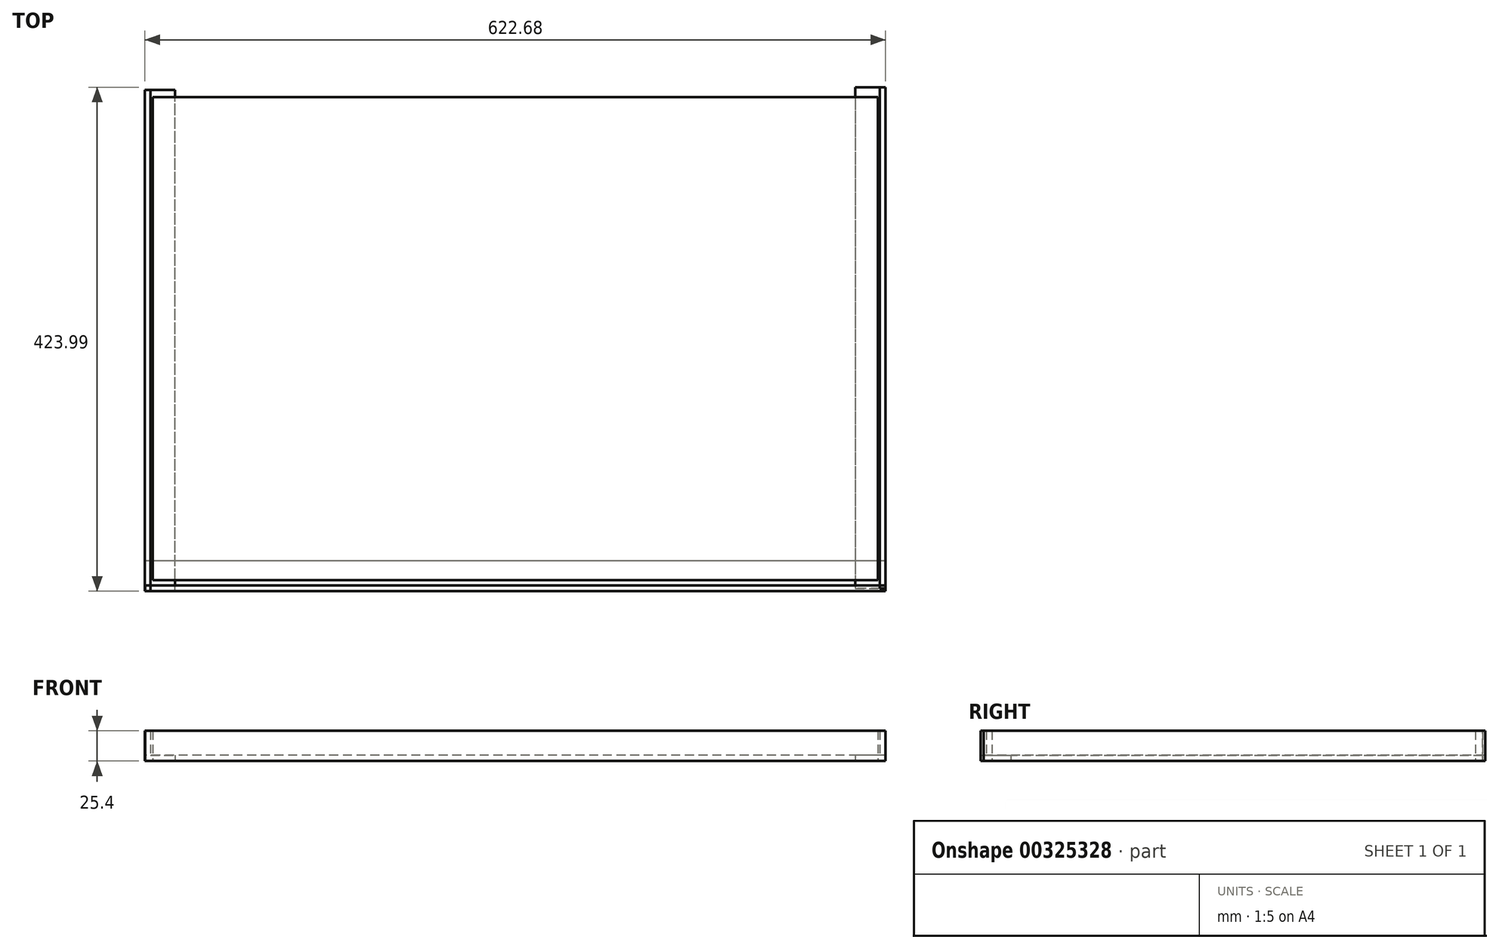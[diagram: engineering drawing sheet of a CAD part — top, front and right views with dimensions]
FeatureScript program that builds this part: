
annotation { "Feature Type Name" : "Feature", "Feature Type Description" : "" }
export const myFeature = defineFeature(function(context is Context, id is Id, definition is map)
    precondition{}
    {
        {
            var Q0;
            Q0=qCreatedBy(makeId("Right.planeOp"),FACE);
            var sketch = newSketch(context, id + "F0", { "sketchPlane" : qUnion([Q0])});
            skLineSegment(sketch, "E0", {"start": v(0, 0) * mm, "end": v(0, 25.4) * mm});
            skLineSegment(sketch, "E1", {"start": v(0, 25.4) * mm, "end": v(4.76, 25.4) * mm});
            skLineSegment(sketch, "E2", {"start": v(4.76, 25.4) * mm, "end": v(4.76, 4.76) * mm});
            skLineSegment(sketch, "E3", {"start": v(4.76, 4.76) * mm, "end": v(25.4, 4.76) * mm});
            skLineSegment(sketch, "E4", {"start": v(25.4, 4.76) * mm, "end": v(25.4, 0) * mm});
            skLineSegment(sketch, "E5", {"start": v(25.4, 0) * mm, "end": v(0, 0) * mm});
            skSolve(sketch);
        }
        {
            var Q0;
            Q0=makeQuery(id+"F0.imprint","IMPRINT",FACE,{"disambiguationData":[TD([[makeQuery(id+"F0.imprint","IMPRINT",EDGE,{"derivedFrom":sQuery(id+"F0.wireOp",EDGE,"E0")}),-1.0]])]});
            extrude(context, id + "F1", {"entities" : qUnion([Q0]), "endBound" : BoundingType.SYMMETRIC, "depth" : 622.3 * mm});
        }
        {
            var Q0;
            Q0=makeQuery(id+"F0.imprint","IMPRINT",FACE,{"disambiguationData":[TD([[makeQuery(id+"F0.imprint","IMPRINT",EDGE,{"derivedFrom":sQuery(id+"F0.wireOp",EDGE,"E0")}),-1.0]])]});
            extrude(context, id + "F2", {"entities" : qUnion([Q0]), "endBound" : BoundingType.SYMMETRIC, "depth" : 421.64 * mm});
        }
        {
            var Q0;
            Q0=makeQuery(id+"F2.opExtrude","SWEPT_BODY",BODY,{"disambiguationData":[OSD([sQuery(id+"F0.wireOp",EDGE,"E0"),sQuery(id+"F0.wireOp",EDGE,"E1"),sQuery(id+"F0.wireOp",EDGE,"E2"),sQuery(id+"F0.wireOp",EDGE,"E3"),sQuery(id+"F0.wireOp",EDGE,"E4"),sQuery(id+"F0.wireOp",EDGE,"E5")])]});
            var Q1;
            Q1=sQuery(id+"F0.wireOp",EDGE,"E2");
            transform(context, id + "F3", {"entities" : qUnion([Q0]), "transformType" : TransformType.ROTATION, "transformAxis" : qUnion([Q1]), "angle" : 90 * degree, "makeCopy" : false});
        }
        {
            var Q0;
            Q0=makeQuery(id+"F2.opExtrude","SWEPT_BODY",BODY,{"disambiguationData":[OSD([sQuery(id+"F0.wireOp",EDGE,"E0"),sQuery(id+"F0.wireOp",EDGE,"E1"),sQuery(id+"F0.wireOp",EDGE,"E2"),sQuery(id+"F0.wireOp",EDGE,"E3"),sQuery(id+"F0.wireOp",EDGE,"E4"),sQuery(id+"F0.wireOp",EDGE,"E5")])]});
            transform(context, id + "F4", {"entities" : qUnion([Q0]), "transformType" : TransformType.TRANSLATION_3D, "dx" : -306.58 * mm, "dy" : 0 * mm, "dz" : 0 * mm, "makeCopy" : false});
        }
        {
            var Q0;
            Q0=makeQuery(id+"F1.opExtrude","SWEPT_BODY",BODY,{"disambiguationData":[OSD([sQuery(id+"F0.wireOp",EDGE,"E0"),sQuery(id+"F0.wireOp",EDGE,"E1"),sQuery(id+"F0.wireOp",EDGE,"E2"),sQuery(id+"F0.wireOp",EDGE,"E3"),sQuery(id+"F0.wireOp",EDGE,"E4"),sQuery(id+"F0.wireOp",EDGE,"E5")])]});
            transform(context, id + "F5", {"entities" : qUnion([Q0]), "transformType" : TransformType.TRANSLATION_3D, "dx" : 0 * mm, "dy" : -206.25 * mm, "dz" : 0 * mm, "makeCopy" : false});
        }
        {
            var Q0;
            Q0=makeQuery(id+"F2.opExtrude","SWEPT_BODY",BODY,{"disambiguationData":[OSD([sQuery(id+"F0.wireOp",EDGE,"E0"),sQuery(id+"F0.wireOp",EDGE,"E1"),sQuery(id+"F0.wireOp",EDGE,"E2"),sQuery(id+"F0.wireOp",EDGE,"E3"),sQuery(id+"F0.wireOp",EDGE,"E4"),sQuery(id+"F0.wireOp",EDGE,"E5")])]});
            var Q1;
            Q1=makeQuery(id+"F1.opExtrude","CAP_EDGE",EDGE,{"disambiguationData":[OSD([sQuery(id+"F0.wireOp",EDGE,"E0")])],"isStart":true});
            transform(context, id + "F6", {"entities" : qUnion([Q0]), "transformType" : TransformType.ROTATION, "transformAxis" : qUnion([Q1]), "angle" : 180 * degree, "oppositeDirection" : true, "makeCopy" : true});
        }
        {
            var Q0;
            Q0=makeQuery(id+"F6.opPattern","COPY",BODY,{"derivedFrom":makeQuery(id+"F2.opExtrude","SWEPT_BODY",BODY,{"disambiguationData":[OSD([sQuery(id+"F0.wireOp",EDGE,"E0"),sQuery(id+"F0.wireOp",EDGE,"E1"),sQuery(id+"F0.wireOp",EDGE,"E2"),sQuery(id+"F0.wireOp",EDGE,"E3"),sQuery(id+"F0.wireOp",EDGE,"E4"),sQuery(id+"F0.wireOp",EDGE,"E5")])]}),"instanceName":"1"});
            transform(context, id + "F7", {"entities" : qUnion([Q0]), "transformType" : TransformType.TRANSLATION_3D, "dx" : 622.3 * mm, "dy" : 424.18 * mm, "dz" : 0 * mm, "makeCopy" : false});
        }
        {
            var Q0;
            Q0=qCreatedBy(makeId("Top.planeOp"),FACE);
            var sketch = newSketch(context, id + "F8", { "sketchPlane" : qUnion([Q0])});
            skLineSegment(sketch, "E6.bottom", {"start": v(304.8, 203.2) * mm, "end": v(-304.8, 203.2) * mm});
            skLineSegment(sketch, "E6.top", {"start": v(304.8, -203.2) * mm, "end": v(-304.8, -203.2) * mm});
            skLineSegment(sketch, "E6.left", {"start": v(304.8, 203.2) * mm, "end": v(304.8, -203.2) * mm});
            skLineSegment(sketch, "E6.right", {"start": v(-304.8, 203.2) * mm, "end": v(-304.8, -203.2) * mm});
            skPoint(sketch, "E6.middle", {"position": v(0, 0) * mm});
            skSolve(sketch);
        }
        {
            var Q0;
            Q0=makeQuery(id+"F8.imprint","IMPRINT",FACE,{"disambiguationData":[TD([[makeQuery(id+"F8.imprint","IMPRINT",EDGE,{"derivedFrom":sQuery(id+"F8.wireOp",EDGE,"E6.bottom")}),1.0]])]});
            extrude(context, id + "F9", {"entities" : qUnion([Q0]), "depth" : 25.4 * mm});
        }
        {
            var Q0;
            Q0=makeQuery(id+"F9.opExtrude","SWEPT_BODY",BODY,{"disambiguationData":[OSD([sQuery(id+"F8.wireOp",EDGE,"E6.bottom"),sQuery(id+"F8.wireOp",EDGE,"E6.top"),sQuery(id+"F8.wireOp",EDGE,"E6.left"),sQuery(id+"F8.wireOp",EDGE,"E6.right")])]});
            transform(context, id + "F10", {"entities" : qUnion([Q0]), "transformType" : TransformType.TRANSLATION_3D, "dx" : 0 * mm, "dy" : 6.35 * mm, "dz" : 0 * mm, "makeCopy" : false});
        }
    });
